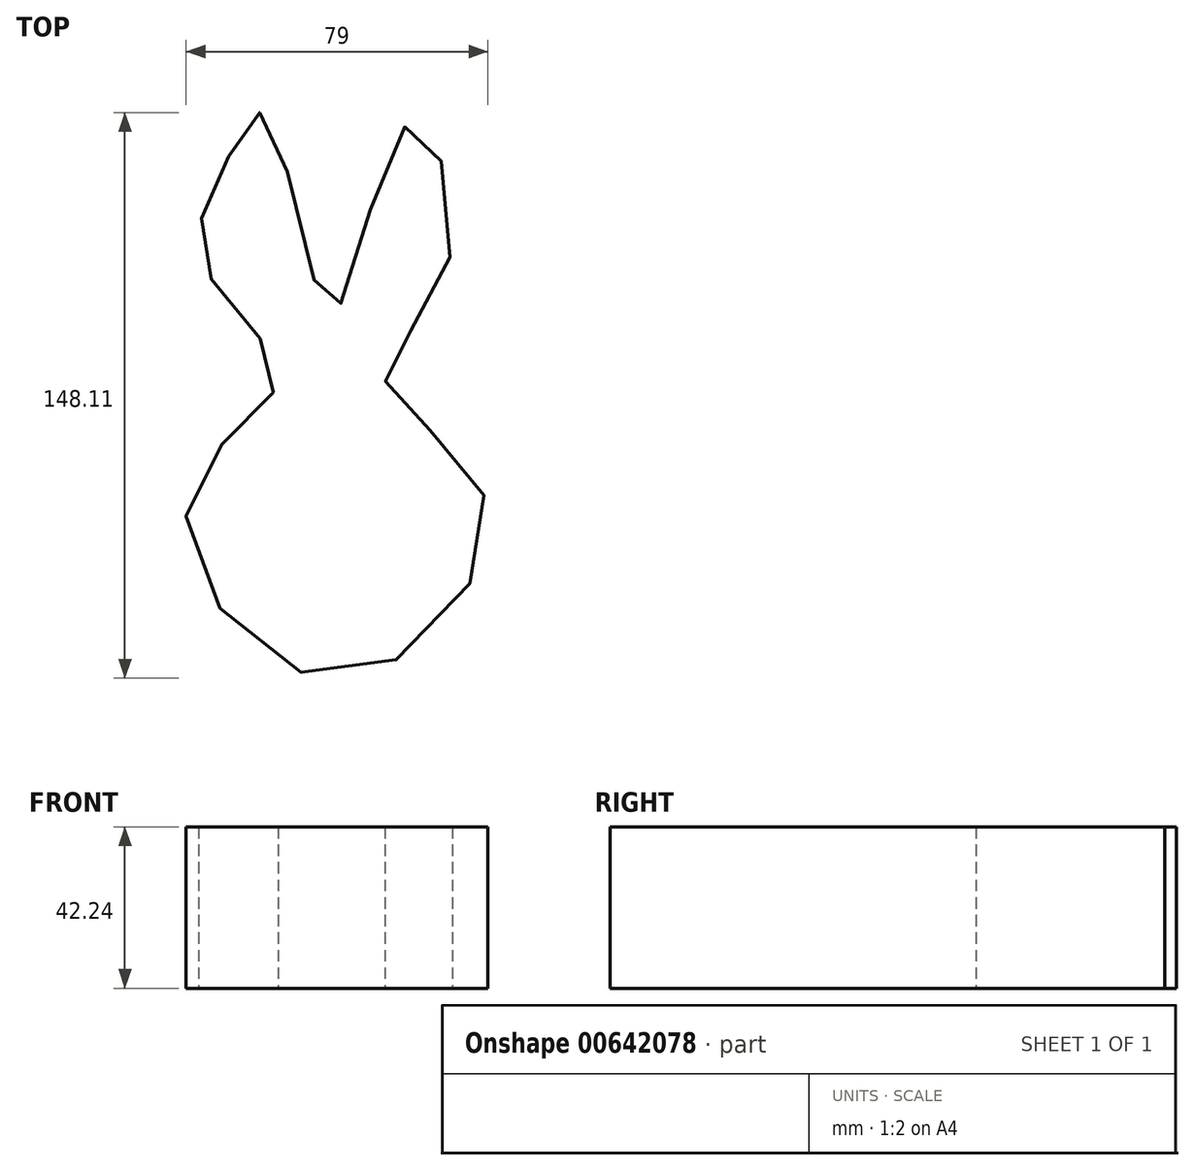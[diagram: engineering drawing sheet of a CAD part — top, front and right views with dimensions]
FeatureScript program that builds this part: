
annotation { "Feature Type Name" : "Feature", "Feature Type Description" : "" }
export const myFeature = defineFeature(function(context is Context, id is Id, definition is map)
    precondition{}
    {
        {
            var Q0;
            Q0=qCreatedBy(makeId("Top.planeOp"),FACE);
            var sketch = newSketch(context, id + "F0", { "sketchPlane" : qUnion([Q0])});
            skFitSpline(sketch, "E0", {"points": [v(-26.9, 40.87) * mm, v(-17.02, 51.52) * mm, v(0, 0) * mm, v(19.6, 48.96) * mm, v(30.63, 13.06) * mm, v(14.1, -18.08) * mm, v(40.5, -50.35) * mm, v(0, -95.74) * mm, v(-37.53, -48.34) * mm, v(-14.07, -17.35) * mm, v(-33.5, 12.34) * mm, v(-26.9, 40.87) * mm]});
            skSolve(sketch);
        }
        {
            var Q0;
            Q0=makeQuery(id+"F0.imprint","IMPRINT",FACE,{"disambiguationData":[TD([[makeQuery(id+"F0.imprint","IMPRINT",EDGE,{"derivedFrom":sQuery(id+"F0.wireOp",EDGE,"E0")}),-1.0]])]});
            extrude(context, id + "F1", {"entities" : qUnion([Q0]), "depth" : 42.24 * mm, "offsetDistance" : 25.4 * mm});
        }
    });
